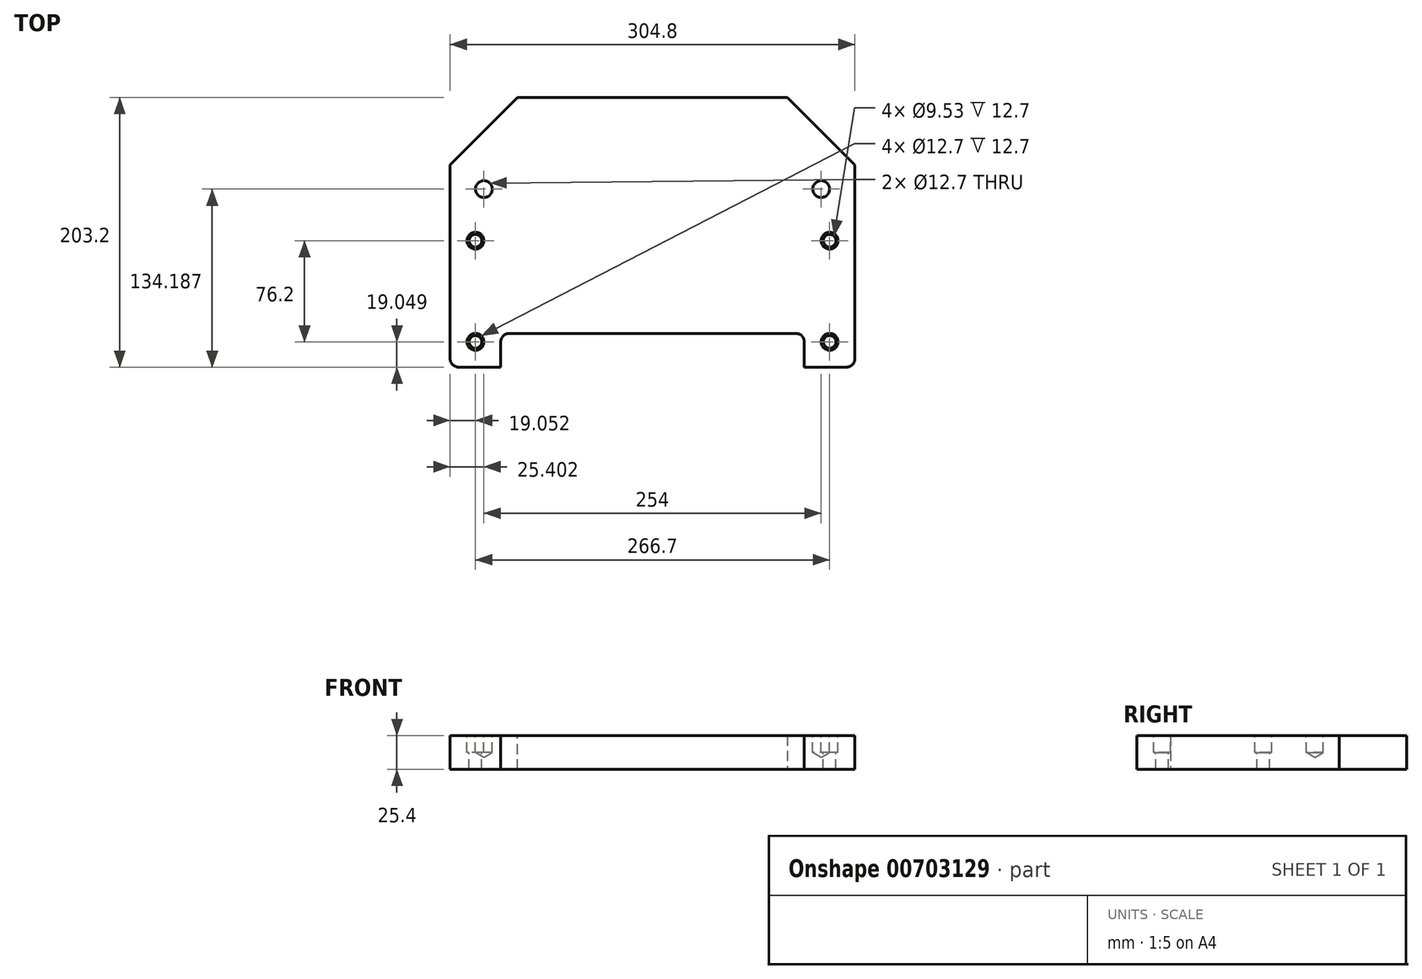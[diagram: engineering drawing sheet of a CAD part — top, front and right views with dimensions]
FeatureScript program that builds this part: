
annotation { "Feature Type Name" : "Feature", "Feature Type Description" : "" }
export const myFeature = defineFeature(function(context is Context, id is Id, definition is map)
    precondition{}
    {
        {
            var Q0;
            Q0=qCreatedBy(makeId("Top.planeOp"),FACE);
            var sketch = newSketch(context, id + "F0", { "sketchPlane" : qUnion([Q0])});
            skLineSegment(sketch, "E0.bottom", {"start": v(-151.45, -100.14) * mm, "end": v(153.35, -100.14) * mm});
            skLineSegment(sketch, "E0.top", {"start": v(-151.45, 103.06) * mm, "end": v(153.35, 103.06) * mm});
            skLineSegment(sketch, "E0.left", {"start": v(-151.45, -100.14) * mm, "end": v(-151.45, 103.06) * mm});
            skLineSegment(sketch, "E0.right", {"start": v(153.35, -100.14) * mm, "end": v(153.35, 103.06) * mm});
            skSolve(sketch);
        }
        {
            var Q0;
            Q0=makeQuery(id+"F0.imprint","IMPRINT",FACE,{"disambiguationData":[TD([[makeQuery(id+"F0.imprint","IMPRINT",EDGE,{"derivedFrom":sQuery(id+"F0.wireOp",EDGE,"E0.bottom")}),1.0]])]});
            extrude(context, id + "F1", {"entities" : qUnion([Q0]), "depth" : 25.4 * mm, "offsetDistance" : 25.4 * mm});
        }
        {
            var Q0;
            Q0=makeQuery(id+"F1.opExtrude","SWEPT_FACE",FACE,{"disambiguationData":[OSD([sQuery(id+"F0.wireOp",EDGE,"E0.bottom")])]});
            var sketch = newSketch(context, id + "F2", { "sketchPlane" : qUnion([Q0])});
            skSolve(sketch);
        }
        {
            var Q0;
            Q0=makeQuery(id+"F1.opExtrude","SWEPT_EDGE",EDGE,{"disambiguationData":[OSD([sQuery(id+"F0.wireOp",EDGE,"E0.top"),sQuery(id+"F0.wireOp",EDGE,"E0.left")])]});
            var Q1;
            Q1=makeQuery(id+"F1.opExtrude","SWEPT_EDGE",EDGE,{"disambiguationData":[OSD([sQuery(id+"F0.wireOp",EDGE,"E0.top"),sQuery(id+"F0.wireOp",EDGE,"E0.right")])]});
            chamfer(context, id + "F3", {"entities" : qUnion([Q0, Q1]), "width" : 50.8 * mm, "tangentPropagation" : true});
        }
        {
            var Q0;
            {var subQ0=sQuery(id+"F0.wireOp",EDGE,"E0.bottom");Q0=makeQuery(id+"F2.imprint","IMPRINT",FACE,{"disambiguationData":[TD([[makeQuery(id+"F2.imprint","IMPRINT",EDGE,{"derivedFrom":makeQuery(id+"F1.opExtrude","CAP_EDGE",EDGE,{"disambiguationData":[OSD([subQ0])],"isStart":true})}),1.0]])]});}
            var sketch = newSketch(context, id + "F4", { "sketchPlane" : qUnion([Q0])});
            skLineSegment(sketch, "E1.0", {"start": v(-113.35, 25.4) * mm, "end": v(115.25, 25.4) * mm});
            skLineSegment(sketch, "E2.0", {"start": v(-113.35, 0) * mm, "end": v(115.25, 0) * mm});
            skLineSegment(sketch, "E3.left", {"start": v(-113.35, 25.4) * mm, "end": v(-113.35, 0) * mm});
            skLineSegment(sketch, "E3.right", {"start": v(115.25, 25.4) * mm, "end": v(115.25, 0) * mm});
            skPoint(sketch, "E4.orphan", {"position": v(-151.45, 25.4) * mm});
            skPoint(sketch, "E5.orphan", {"position": v(-151.45, 0) * mm});
            skPoint(sketch, "E6.orphan", {"position": v(153.35, 25.4) * mm});
            skPoint(sketch, "E7.orphan", {"position": v(153.35, 0) * mm});
            skSolve(sketch);
        }
        {
            var Q0;
            Q0=qSketchRegion(id+"F4",true);
            extrude(context, id + "F5", {"entities" : qUnion([Q0]), "operationType" : NewBodyOperationType.REMOVE, "oppositeDirection" : true, "depth" : 25.4 * mm, "offsetDistance" : 25.4 * mm});
        }
        {
            var Q0;
            Q0=makeQuery(id+"F5.boolean.opBoolean","COPY",EDGE,{"derivedFrom":makeQuery(id+"F5.opExtrude","CAP_EDGE",EDGE,{"disambiguationData":[OSD([sQuery(id+"F4.wireOp",EDGE,"E3.left")])],"isStart":true})});
            var Q1;
            Q1=makeQuery(id+"F5.boolean.opBoolean","COPY",EDGE,{"derivedFrom":makeQuery(id+"F5.opExtrude","CAP_EDGE",EDGE,{"disambiguationData":[OSD([sQuery(id+"F4.wireOp",EDGE,"E3.left")])],"isStart":false})});
            var Q2;
            Q2=makeQuery(id+"F5.boolean.opBoolean","COPY",EDGE,{"derivedFrom":makeQuery(id+"F5.opExtrude","CAP_EDGE",EDGE,{"disambiguationData":[OSD([sQuery(id+"F4.wireOp",EDGE,"E3.right")])],"isStart":false})});
            var Q3;
            Q3=makeQuery(id+"F5.boolean.opBoolean","COPY",EDGE,{"derivedFrom":makeQuery(id+"F5.opExtrude","CAP_EDGE",EDGE,{"disambiguationData":[OSD([sQuery(id+"F4.wireOp",EDGE,"E3.right")])],"isStart":true})});
            var Q4;
            Q4=makeQuery(id+"F1.opExtrude","SWEPT_EDGE",EDGE,{"disambiguationData":[OSD([sQuery(id+"F0.wireOp",EDGE,"E0.bottom"),sQuery(id+"F0.wireOp",EDGE,"E0.right")])]});
            var Q5;
            Q5=makeQuery(id+"F1.opExtrude","SWEPT_EDGE",EDGE,{"disambiguationData":[OSD([sQuery(id+"F0.wireOp",EDGE,"E0.bottom"),sQuery(id+"F0.wireOp",EDGE,"E0.left")])]});
            fillet(context, id + "F6", {"entities" : qUnion([Q0, Q1, Q2, Q3, Q4, Q5]), "radius" : 6.35 * mm, "tangentPropagation" : true, "allowEdgeOverflow" : false});
        }
        {
            var Q0;
            Q0=makeQuery(id+"F1.opExtrude","CAP_FACE",FACE,{"disambiguationData":[OSD([sQuery(id+"F0.wireOp",EDGE,"E0.bottom"),sQuery(id+"F0.wireOp",EDGE,"E0.top"),sQuery(id+"F0.wireOp",EDGE,"E0.left"),sQuery(id+"F0.wireOp",EDGE,"E0.right")])],"isStart":false});
            var sketch = newSketch(context, id + "F7", { "sketchPlane" : qUnion([Q0])});
            skPoint(sketch, "E8", {"position": v(-132.4, -81.1) * mm});
            skPoint(sketch, "E9", {"position": v(134.3, -81.1) * mm});
            skPoint(sketch, "E10", {"position": v(-132.4, -4.9) * mm});
            skPoint(sketch, "E11", {"position": v(134.3, -4.9) * mm});
            skSolve(sketch);
        }
        {
            var Q0;
            Q0=sQuery(id+"F7.wireOp",VERTEX,"E8");
            var Q1;
            Q1=sQuery(id+"F7.wireOp",VERTEX,"E10");
            var Q2;
            Q2=sQuery(id+"F7.wireOp",VERTEX,"E11");
            var Q3;
            Q3=sQuery(id+"F7.wireOp",VERTEX,"E9");
            var Q4;
            Q4=makeQuery(id+"F1.opExtrude","SWEPT_BODY",BODY,{"disambiguationData":[OSD([sQuery(id+"F0.wireOp",EDGE,"E0.bottom"),sQuery(id+"F0.wireOp",EDGE,"E0.top"),sQuery(id+"F0.wireOp",EDGE,"E0.left"),sQuery(id+"F0.wireOp",EDGE,"E0.right")])]});
            hole(context, id + "F8", {"style" : HoleStyle.C_BORE, "endStyle" : HoleEndStyle.THROUGH, "holeDiameter" : 9.52 * mm, "cBoreDiameter" : 12.7 * mm, "cBoreDepth" : 12.7 * mm, "majorDiameter" : 6.35 * mm, "isTappedThrough" : true, "tappedDepth" : 12.7 * mm, "tapClearance" : 3, "locations" : qUnion([Q0, Q1, Q2, Q3]), "scope" : qUnion([Q4])});
        }
        {
            var Q0;
            Q0=makeQuery(id+"F1.opExtrude","CAP_FACE",FACE,{"disambiguationData":[OSD([sQuery(id+"F0.wireOp",EDGE,"E0.bottom"),sQuery(id+"F0.wireOp",EDGE,"E0.top"),sQuery(id+"F0.wireOp",EDGE,"E0.left"),sQuery(id+"F0.wireOp",EDGE,"E0.right")])],"isStart":false});
            var sketch = newSketch(context, id + "F9", { "sketchPlane" : qUnion([Q0])});
            skPoint(sketch, "E12", {"position": v(-126.05, 34.05) * mm});
            skPoint(sketch, "E13.1.0.0", {"position": v(127.95, 34.05) * mm});
            skLineSegment(sketch, "E13.direction1", {"start": v(-126.05, 34.05) * mm, "end": v(127.95, 34.05) * mm, "construction": true});
            skSolve(sketch);
        }
        {
            var Q0;
            Q0=sQuery(id+"F9.wireOp",VERTEX,"E12");
            var Q1;
            Q1=sQuery(id+"F9.wireOp",VERTEX,"E13.1.0.0");
            var Q2;
            Q2=makeQuery(id+"F1.opExtrude","SWEPT_BODY",BODY,{"disambiguationData":[OSD([sQuery(id+"F0.wireOp",EDGE,"E0.bottom"),sQuery(id+"F0.wireOp",EDGE,"E0.top"),sQuery(id+"F0.wireOp",EDGE,"E0.left"),sQuery(id+"F0.wireOp",EDGE,"E0.right")])]});
            hole(context, id + "F10", {"style" : HoleStyle.SIMPLE, "endStyle" : HoleEndStyle.BLIND, "holeDiameter" : 12.7 * mm, "majorDiameter" : 6.35 * mm, "holeDepth" : 12.7 * mm, "isTappedThrough" : true, "tappedDepth" : 12.7 * mm, "tapClearance" : 3, "locations" : qUnion([Q0, Q1]), "scope" : qUnion([Q2])});
        }
    });
